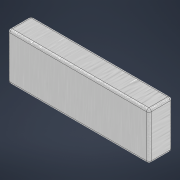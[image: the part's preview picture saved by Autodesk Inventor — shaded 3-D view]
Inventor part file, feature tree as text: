
AUTODESK INVENTOR PART (.ipt)
format: ipt  version: 2022 (Build 260153070, 153G)  size: 274,432 bytes
history: native  units: mm
features: other x1, extrude x1, fillet x1, sketch x1
ambient origin geometry x8: Origin, YZ Plane, XZ Plane, XY Plane, X Axis, Y Axis, Z Axis, Center Point
bodies: Body1 (feature_tree)
feature tree (4):
  other  "Твердое тело1"
  extrude  "Выдавливание1"  Depth=60.0mm
  fillet  "Сопряжение1"  Radius=20.0mm
  sketch  "Эскиз1"
